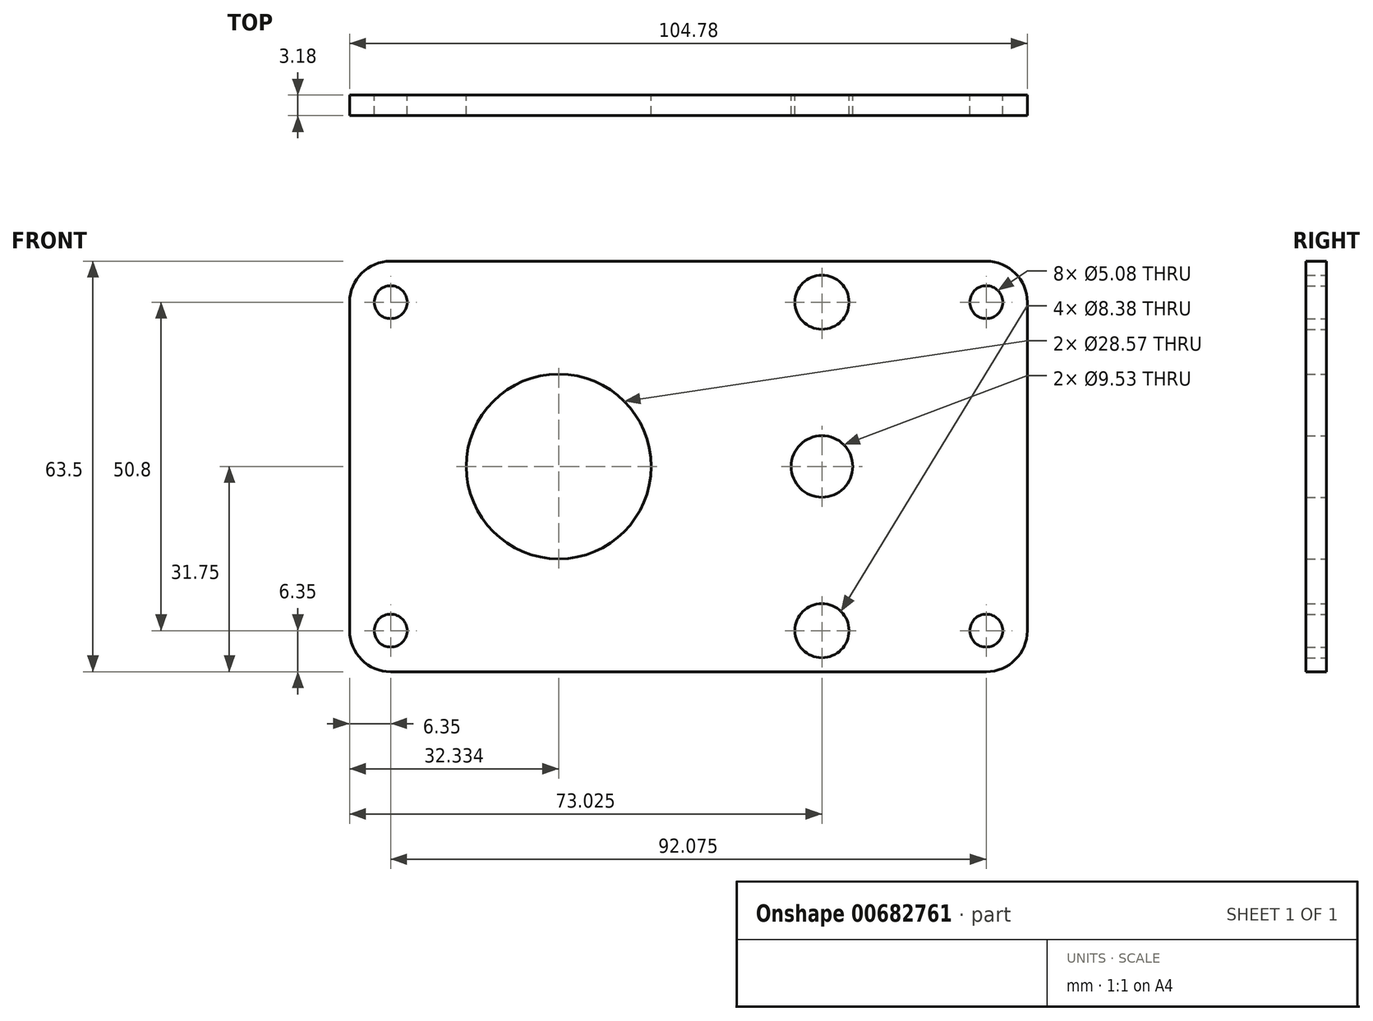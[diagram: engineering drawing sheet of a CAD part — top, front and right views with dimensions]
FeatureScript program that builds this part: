
annotation { "Feature Type Name" : "Feature", "Feature Type Description" : "" }
export const myFeature = defineFeature(function(context is Context, id is Id, definition is map)
    precondition{}
    {
        {
            var Q0;
            Q0=qCreatedBy(makeId("Front.planeOp"),FACE);
            var sketch = newSketch(context, id + "F0", { "sketchPlane" : qUnion([Q0])});
            skLineSegment(sketch, "E0.bottom", {"start": v(6.35, 0) * mm, "end": v(98.43, 0) * mm});
            skLineSegment(sketch, "E0.top", {"start": v(6.35, 63.5) * mm, "end": v(98.43, 63.5) * mm});
            skLineSegment(sketch, "E0.left", {"start": v(0, 6.35) * mm, "end": v(0, 57.15) * mm});
            skLineSegment(sketch, "E0.right", {"start": v(104.78, 6.35) * mm, "end": v(104.78, 57.15) * mm});
            skPoint(sketch, "E1.visualSharp", {"position": v(0, 63.5) * mm});
            skArc(sketch, "E1.filletArc", {"start": v(6.35, 63.5) * mm, "mid": v(1.86, 61.64) * mm, "end": v(0, 57.15) * mm});
            skPoint(sketch, "E2.visualSharp", {"position": v(0, 0) * mm});
            skArc(sketch, "E2.filletArc", {"start": v(0, 6.35) * mm, "mid": v(1.86, 1.86) * mm, "end": v(6.35, 0) * mm});
            skPoint(sketch, "E3.visualSharp", {"position": v(104.78, 0) * mm});
            skArc(sketch, "E3.filletArc", {"start": v(98.43, 0) * mm, "mid": v(102.92, 1.86) * mm, "end": v(104.77, 6.35) * mm});
            skPoint(sketch, "E4.visualSharp", {"position": v(104.78, 63.5) * mm});
            skArc(sketch, "E4.filletArc", {"start": v(104.77, 57.15) * mm, "mid": v(102.92, 61.64) * mm, "end": v(98.43, 63.5) * mm});
            skCircle(sketch, "E5", {"center": v(32.33, 31.75) * mm, "radius": 14.29 * mm});
            skCircle(sketch, "E6", {"center": v(73.03, 57.15) * mm, "radius": 4.2 * mm});
            skCircle(sketch, "E7", {"center": v(73.03, 31.75) * mm, "radius": 4.76 * mm});
            skCircle(sketch, "E8", {"center": v(73.03, 6.35) * mm, "radius": 4.2 * mm});
            skCircle(sketch, "E9", {"center": v(6.35, 57.15) * mm, "radius": 2.54 * mm});
            skCircle(sketch, "E10.0.1.0", {"center": v(6.35, 6.35) * mm, "radius": 2.54 * mm});
            skCircle(sketch, "E10.1.0.0", {"center": v(98.42, 57.15) * mm, "radius": 2.54 * mm});
            skCircle(sketch, "E10.1.1.0", {"center": v(98.42, 6.35) * mm, "radius": 2.54 * mm});
            skLineSegment(sketch, "E10.direction1", {"start": v(6.35, 57.15) * mm, "end": v(98.42, 57.15) * mm, "construction": true});
            skLineSegment(sketch, "E10.direction2", {"start": v(6.35, 57.15) * mm, "end": v(6.35, 6.35) * mm, "construction": true});
            skSolve(sketch);
        }
        {
            var Q0;
            Q0=makeQuery(id+"F0.imprint","IMPRINT",FACE,{"disambiguationData":[TD([[makeQuery(id+"F0.imprint","IMPRINT",EDGE,{"derivedFrom":sQuery(id+"F0.wireOp",EDGE,"E0.bottom")}),1.0]])]});
            extrude(context, id + "F1", {"entities" : qUnion([Q0]), "depth" : 3.17 * mm, "offsetDistance" : 25.4 * mm});
        }
    });
